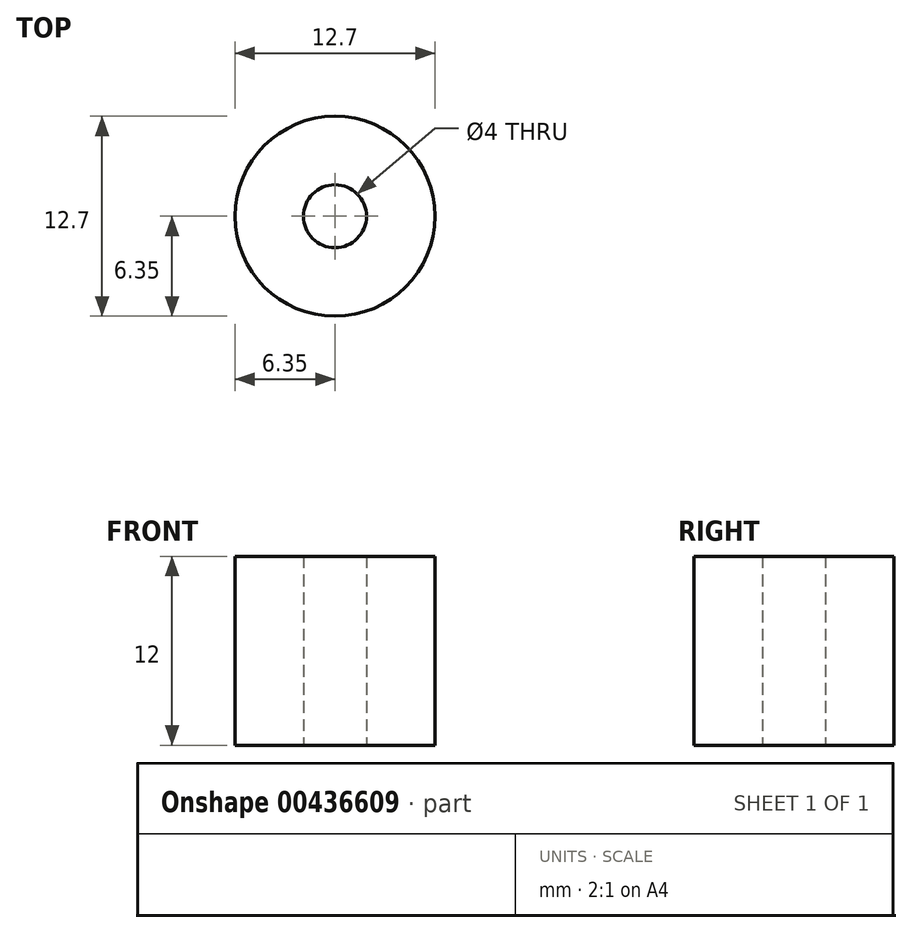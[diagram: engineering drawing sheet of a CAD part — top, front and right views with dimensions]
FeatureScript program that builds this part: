
annotation { "Feature Type Name" : "Feature", "Feature Type Description" : "" }
export const myFeature = defineFeature(function(context is Context, id is Id, definition is map)
    precondition{}
    {
        {
            var Q0;
            Q0=qCreatedBy(makeId("Top.planeOp"),FACE);
            var sketch = newSketch(context, id + "F0", { "sketchPlane" : qUnion([Q0])});
            skCircle(sketch, "E0", {"center": v(0, 0) * mm, "radius": 6.35 * mm});
            skCircle(sketch, "E1", {"center": v(0, 0) * mm, "radius": 2 * mm});
            skSolve(sketch);
        }
        {
            var Q0;
            Q0=makeQuery(id+"F0.imprint","IMPRINT",FACE,{"disambiguationData":[TD([[makeQuery(id+"F0.imprint","IMPRINT",EDGE,{"derivedFrom":sQuery(id+"F0.wireOp",EDGE,"E0")}),1.0]])]});
            extrude(context, id + "F1", {"entities" : qUnion([Q0]), "depth" : 12 * mm});
        }
    });
